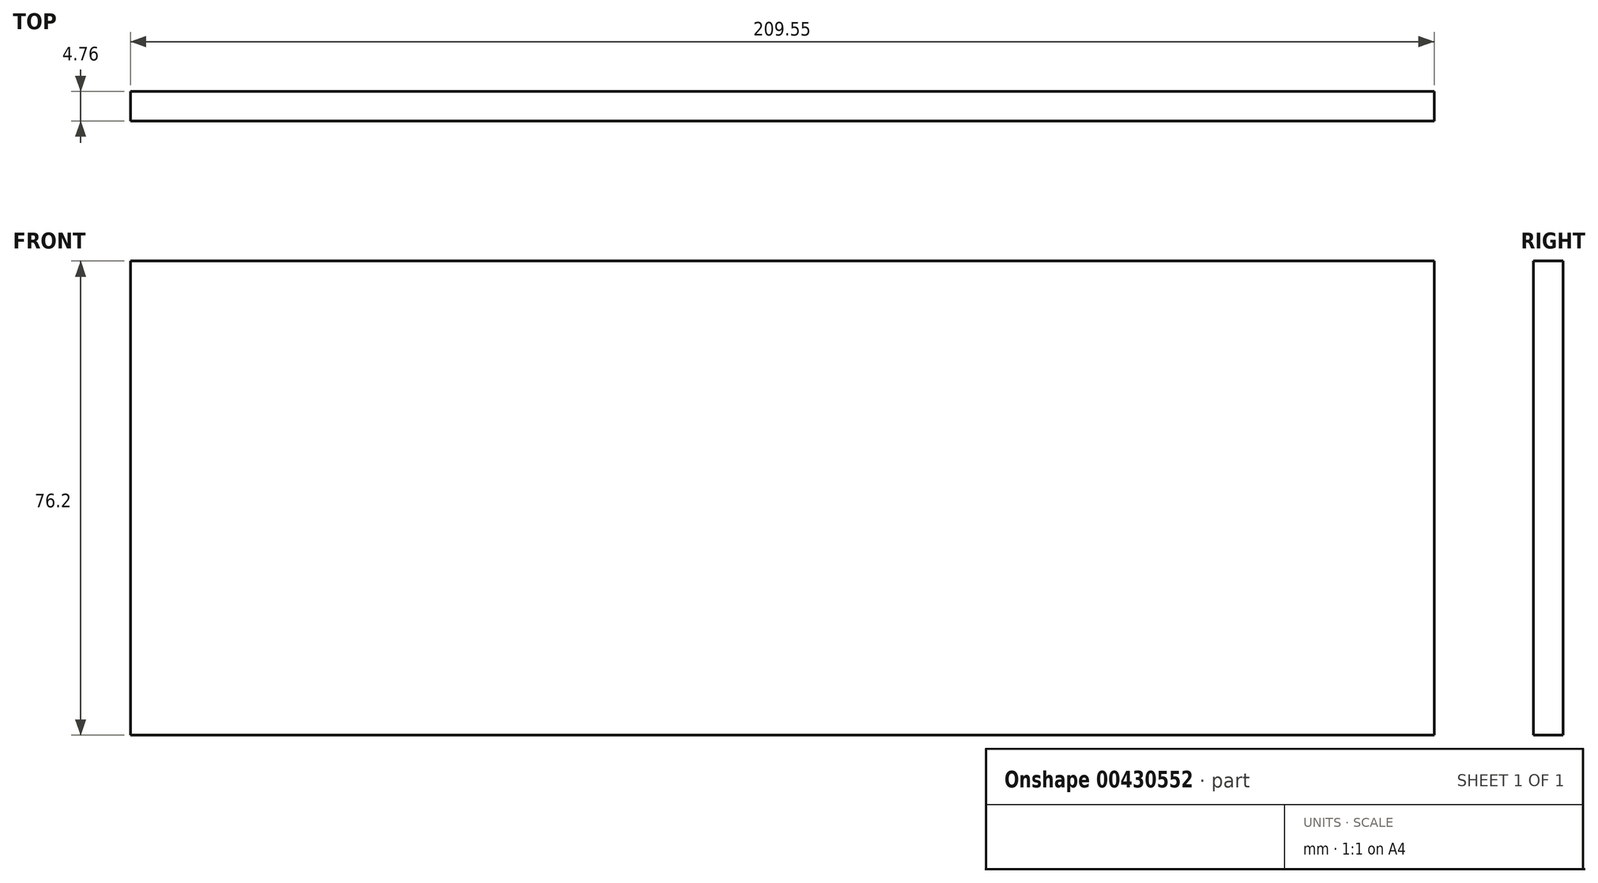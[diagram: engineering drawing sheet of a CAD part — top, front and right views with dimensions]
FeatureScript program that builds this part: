
annotation { "Feature Type Name" : "Feature", "Feature Type Description" : "" }
export const myFeature = defineFeature(function(context is Context, id is Id, definition is map)
    precondition{}
    {
        {
            var Q0;
            Q0=qCreatedBy(makeId("Front.planeOp"),FACE);
            var sketch = newSketch(context, id + "F0", { "sketchPlane" : qUnion([Q0])});
            skLineSegment(sketch, "E0.bottom", {"start": v(-34.62, 22.38) * mm, "end": v(174.93, 22.38) * mm});
            skLineSegment(sketch, "E0.top", {"start": v(-34.62, -53.82) * mm, "end": v(174.93, -53.82) * mm});
            skLineSegment(sketch, "E0.left", {"start": v(-34.62, 22.38) * mm, "end": v(-34.62, -53.82) * mm});
            skLineSegment(sketch, "E0.right", {"start": v(174.93, 22.38) * mm, "end": v(174.93, -53.82) * mm});
            skSolve(sketch);
        }
        {
            var Q0;
            Q0=makeQuery(id+"F0.imprint","IMPRINT",FACE,{"disambiguationData":[TD([[makeQuery(id+"F0.imprint","IMPRINT",EDGE,{"derivedFrom":sQuery(id+"F0.wireOp",EDGE,"E0.bottom")}),-1.0]])]});
            extrude(context, id + "F1", {"entities" : qUnion([Q0]), "depth" : 4.76 * mm});
        }
    });
